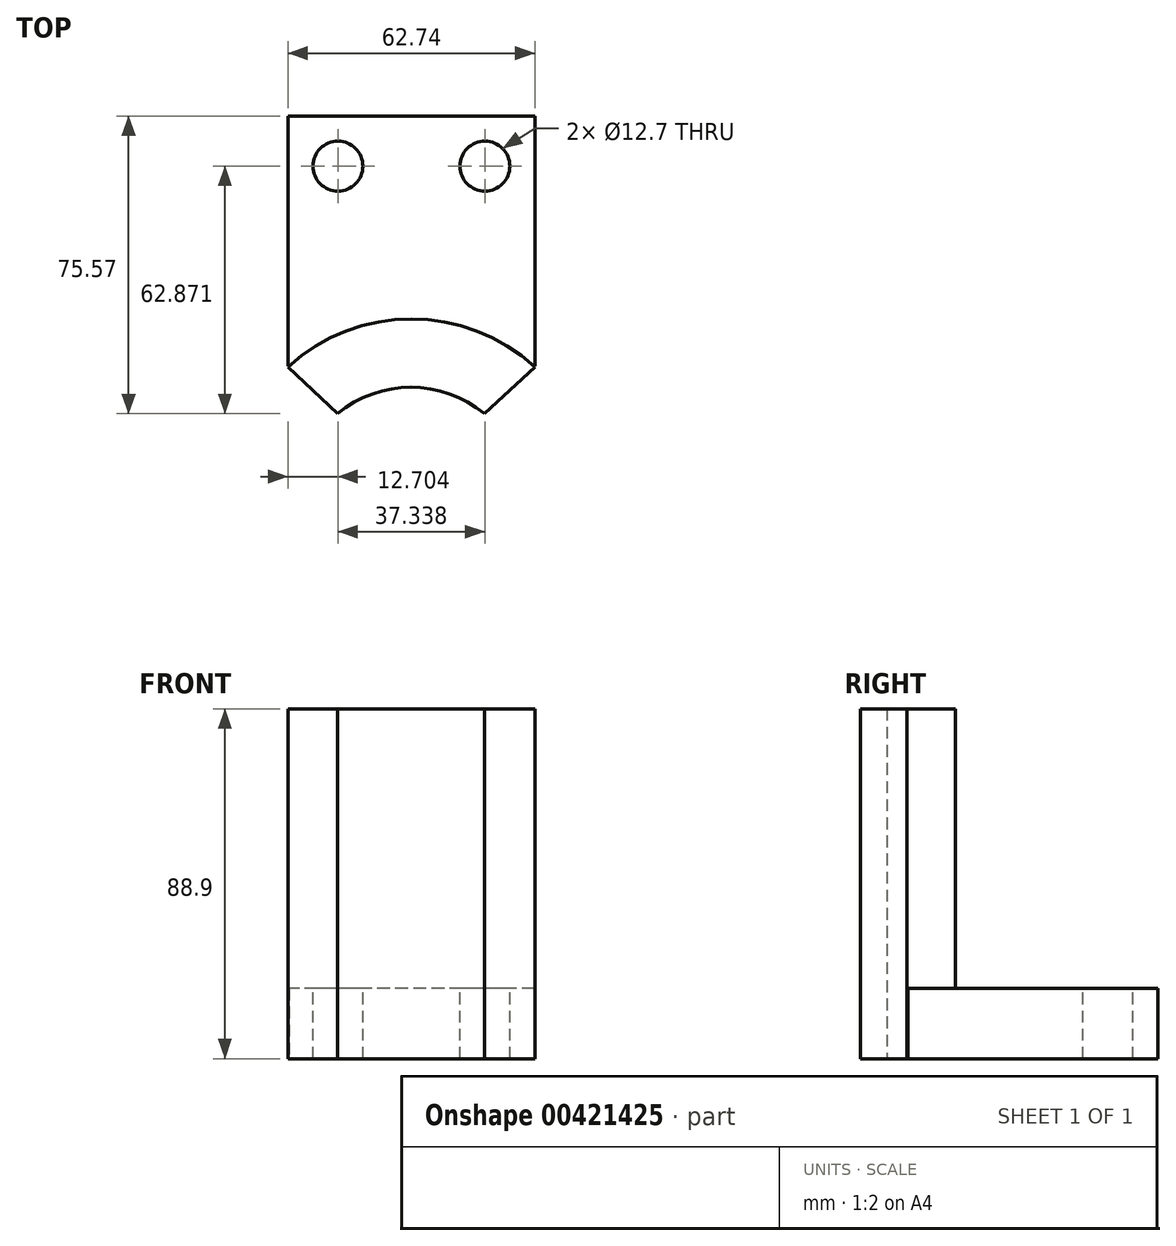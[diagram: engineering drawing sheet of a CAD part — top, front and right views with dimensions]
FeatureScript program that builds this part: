
annotation { "Feature Type Name" : "Feature", "Feature Type Description" : "" }
export const myFeature = defineFeature(function(context is Context, id is Id, definition is map)
    precondition{}
    {
        {
            var Q0;
            Q0=qCreatedBy(makeId("Top.planeOp"),FACE);
            var sketch = newSketch(context, id + "F0", { "sketchPlane" : qUnion([Q0])});
            skArc(sketch, "E0", {"start": v(18.65, 22.65) * mm, "mid": v(0, 29.34) * mm, "end": v(-18.65, 22.65) * mm});
            skArc(sketch, "E1", {"start": v(31.5, 34.49) * mm, "mid": v(0.12, 46.72) * mm, "end": v(-31.25, 34.49) * mm});
            skLineSegment(sketch, "E2", {"start": v(-31.25, 34.49) * mm, "end": v(31.5, 34.49) * mm, "construction": true});
            skLineSegment(sketch, "E3", {"start": v(31.5, 34.49) * mm, "end": v(18.65, 22.65) * mm});
            skLineSegment(sketch, "E4", {"start": v(-31.25, 34.49) * mm, "end": v(-18.65, 22.65) * mm});
            skSolve(sketch);
        }
        {
            var Q0;
            Q0 = qSketchRegion(id + "F0", true);
            extrude(context, id + "F1", {"entities" : qUnion([Q0]), "depth" : 88.9 * mm});
        }
        {
            var Q0;
            Q0=qCreatedBy(makeId("Front.planeOp"),FACE);
            cPlane(context, id + "F2", {"entities" : qUnion([Q0]), "cplaneType" : CPlaneType.OFFSET, "offset" : 34.72 * mm, "oppositeDirection" : true, "width" : 152.4 * mm, "height" : 152.4 * mm});
        }
        {
            var Q0;
            Q0=qCreatedBy(id+"F2.planeOp",FACE);
            var sketch = newSketch(context, id + "F3", { "sketchPlane" : qUnion([Q0])});
            skLineSegment(sketch, "E5.0.0", {"start": v(31.5, 0) * mm, "end": v(-31.25, 0) * mm});
            skPoint(sketch, "E5.0.2.end.orphan", {"position": v(31.5, 88.9) * mm});
            skPoint(sketch, "E5.0.1.end.orphan", {"position": v(-31.25, 88.9) * mm});
            skLineSegment(sketch, "E6.top", {"start": v(31.5, 17.83) * mm, "end": v(-31.25, 17.83) * mm});
            skLineSegment(sketch, "E6.left", {"start": v(31.5, 0) * mm, "end": v(31.5, 17.83) * mm});
            skLineSegment(sketch, "E6.right", {"start": v(-31.25, 0) * mm, "end": v(-31.25, 17.83) * mm});
            skSolve(sketch);
        }
        {
            var Q0;
            Q0 = qSketchRegion(id + "F3", true);
            extrude(context, id + "F4", {"entities" : qUnion([Q0]), "operationType" : NewBodyOperationType.ADD, "oppositeDirection" : true, "depth" : 63.5 * mm});
        }
        {
            var Q0;
            {var subQ0=sQuery(id+"F3.wireOp",EDGE,"E6.right");var subQ1=sQuery(id+"F3.wireOp",EDGE,"E6.left");var subQ2=sQuery(id+"F3.wireOp",EDGE,"E6.top");var subQ3=makeQuery(id+"F4.opExtrude","SWEPT_FACE",FACE,{"disambiguationData":[OSD([subQ2])]});Q0=makeQuery(id+"F4.boolean.opBoolean","SPLIT",FACE,{"disambiguationData":[TD([makeQuery(id+"F1.opExtrude","SWEPT_FACE",FACE,{"disambiguationData":[OSD([sQuery(id+"F0.wireOp",EDGE,"E1")])]}),makeQuery(id+"F1.opExtrude","SWEPT_FACE",FACE,{"disambiguationData":[OSD([sQuery(id+"F0.wireOp",EDGE,"E3")])]}),makeQuery(id+"F1.opExtrude","SWEPT_FACE",FACE,{"disambiguationData":[OSD([sQuery(id+"F0.wireOp",EDGE,"E4")])]}),makeQuery(id+"F4.opExtrude","CAP_FACE",FACE,{"disambiguationData":[OSD([sQuery(id+"F3.wireOp",EDGE,"E5.0.0"),subQ2,subQ1,subQ0])],"isStart":false}),subQ3,makeQuery(id+"F4.opExtrude","SWEPT_FACE",FACE,{"disambiguationData":[OSD([subQ1])]}),makeQuery(id+"F4.opExtrude","SWEPT_FACE",FACE,{"disambiguationData":[OSD([subQ0])]})])],"derivedFrom":subQ3});}
            var sketch = newSketch(context, id + "F5", { "sketchPlane" : qUnion([Q0])});
            skCircle(sketch, "E7", {"center": v(18.8, 85.52) * mm, "radius": 6.35 * mm});
            skCircle(sketch, "E8", {"center": v(-18.55, 85.52) * mm, "radius": 6.35 * mm});
            skSolve(sketch);
        }
        {
            var Q0;
            Q0 = qSketchRegion(id + "F5", true);
            extrude(context, id + "F6", {"entities" : qUnion([Q0]), "operationType" : NewBodyOperationType.REMOVE, "oppositeDirection" : true, "depth" : 25.4 * mm});
        }
    });
